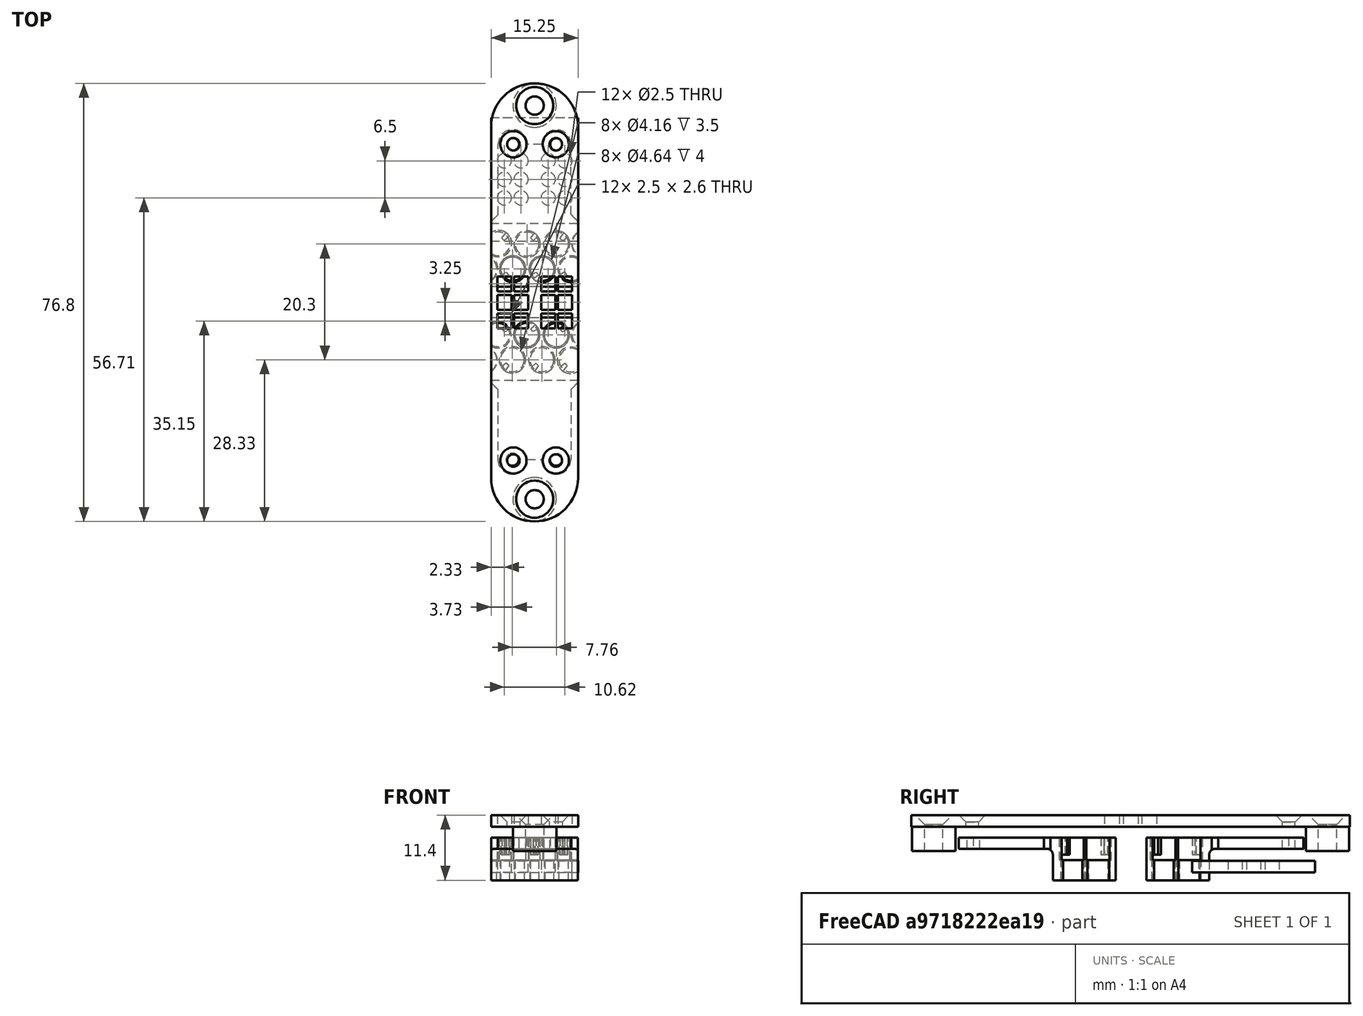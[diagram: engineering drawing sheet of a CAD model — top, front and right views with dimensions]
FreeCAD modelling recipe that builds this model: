
FCSTD DOCUMENT  (FreeCAD 0.16R6706 (Git))
Label: BrailleCell
License: All rights reserved
LicenseURL: http://en.wikipedia.org/wiki/All_rights_reserved
objects: Sketcher::SketchObject×11, PartDesign::Pad×11, PartDesign::Chamfer×5, Part::MultiFuse×5, Mesh::Feature×4, Part::Box×2, Part::Cut×2, PartDesign::Fillet×2
note: 49 computed .brp shape members not serialized (recipe doc carries the construction recipe); baked Part::Feature solids carry a one-line shape summary decoded from their .brp

FEATURE [Sketcher::SketchObject] Sketch001
  sketch-geometry (12):
    g0: LineSegment StartX=0 StartY=0 StartZ=0 EndX=15.232 EndY=0 EndZ=0
    g1: LineSegment StartX=15.232 StartY=0 StartZ=0 EndX=15.232 EndY=-20 EndZ=0
    g2: LineSegment StartX=15.232 StartY=-20 StartZ=0 EndX=0 EndY=-20 EndZ=0
    g3: LineSegment StartX=0 StartY=-20 StartZ=0 EndX=0 EndY=0 EndZ=0
    g4: Circle CenterX=3.8995 CenterY=-16.9419 CenterZ=0 NormalX=0 NormalY=0 NormalZ=1 Radius=1.1
    g5: Circle CenterX=11.3325 CenterY=-16.9419 CenterZ=0 NormalX=0 NormalY=0 NormalZ=1 Radius=1.1
    g6: LineSegment StartX=0 StartY=21.56 StartZ=0 EndX=15.232 EndY=21.56 EndZ=0
    g7: LineSegment StartX=15.232 StartY=21.56 StartZ=0 EndX=15.232 EndY=41.56 EndZ=0
    g8: LineSegment StartX=15.232 StartY=41.56 StartZ=0 EndX=0 EndY=41.56 EndZ=0
    g9: LineSegment StartX=0 StartY=41.56 StartZ=0 EndX=0 EndY=21.56 EndZ=0
    g10: Circle CenterX=3.8995 CenterY=38.5019 CenterZ=0 NormalX=0 NormalY=0 NormalZ=1 Radius=1.1
    g11: Circle CenterX=11.3325 CenterY=38.5019 CenterZ=0 NormalX=0 NormalY=0 NormalZ=1 Radius=1.1
  constraints (34):
    c: Coincident(g0,g1)
    c: Coincident(g1,g2)
    c: Coincident(g2,g3)
    c: Coincident(g3,g0)
    c: Horizontal(g0)
    c: Horizontal(g2)
    c: Vertical(g1)
    c: Vertical(g3)
    c: DistanceX(g-1,g0) = 15.232
    c: DistanceY(g2,g-1) = 20
    c: DistanceY(g4,g-1) = 16.9419
    c: Radius(g4) = 1.1
    c: DistanceY(g5,g-1) = 16.9419
    c: Radius(g5) = 1.1
    c: Coincident(g6,g7)
    c: Coincident(g7,g8)
    c: Coincident(g8,g9)
    c: Coincident(g9,g6)
    c: Horizontal(g6)
    c: Horizontal(g8)
    c: Vertical(g7)
    c: Vertical(g9)
    c: PointOnObject(g6,g-2)
    c: DistanceX(g6,g6) = 15.232
    c: DistanceY(g6,g7) = 20
    c: Radius(g11) = 1.1
    c: Radius(g10) = 1.1
    c: DistanceY(g-1,g10) = 38.5019
    c: DistanceY(g-1,g11) = 38.5019
    c: DistanceX(g6,g10) = 3.8995
    c: DistanceX(g-1,g11) = 11.3325
    c: DistanceX(g-1,g4) = 3.8995
    c: DistanceX(g-1,g5) = 11.3325
    c: DistanceY(g-1,g6) = 21.56
FEATURE [Sketcher::SketchObject] Sketch002
  sketch-geometry (6):
    g0: ArcOfCircle CenterX=7.616 CenterY=41.56 CenterZ=0 NormalX=0 NormalY=0 NormalZ=1 Radius=7.616 StartAngle=0 EndAngle=3.14159
    g1: ArcOfCircle CenterX=7.616 CenterY=-20 CenterZ=0 NormalX=0 NormalY=0 NormalZ=1 Radius=7.616 StartAngle=3.14159 EndAngle=6.28319
    g2: Circle CenterX=7.616 CenterY=45.28 CenterZ=0 NormalX=0 NormalY=0 NormalZ=1 Radius=1.6
    g3: Circle CenterX=7.616 CenterY=-23.72 CenterZ=0 NormalX=0 NormalY=0 NormalZ=1 Radius=1.6
    g4: LineSegment StartX=0 StartY=-20 StartZ=0 EndX=15.232 EndY=-20 EndZ=0
    g5: LineSegment StartX=0 StartY=41.56 StartZ=0 EndX=15.232 EndY=41.56 EndZ=0
  constraints (20):
    c: DistanceY(g-1,g0) = 41.56
    c: DistanceY(g-1,g0) = 41.56
    c: DistanceY(g-1,g0) = 41.56
    c: DistanceX(g-1,g0) = 7.616
    c: DistanceY(g1,g-1) = 20
    c: DistanceX(g-1,g1) = 7.616
    c: Radius(g2) = 1.6
    c: DistanceY(g-1,g2) = 45.28
    c: DistanceX(g-1,g2) = 7.616
    c: DistanceX(g1,g3) = 7.616
    c: Radius(g3) = 1.6
    c: DistanceY(g3,g-1) = 23.72
    c: Coincident(g4,g1)
    c: Coincident(g4,g1)
    c: Horizontal(g4)
    c: Coincident(g5,g0)
    c: Coincident(g5,g0)
    c: DistanceX(g-1,g0) = 0
    c: DistanceX(g-1,g1) = 0
    c: DistanceY(g1,g1) = 0
FEATURE [PartDesign::Pad] Pad
  Length = 2
  Length2 = 100
  Sketch = -> Sketch002
  Type = 0
FEATURE [PartDesign::Pad] Pad001
  Length = 2
  Length2 = 100
  Sketch = -> Sketch001
  Type = 0
FEATURE [Sketcher::SketchObject] Sketch004
  sketch-geometry (16):
    g0: LineSegment StartX=0 StartY=0 StartZ=0 EndX=15.232 EndY=0 EndZ=0
    g1: LineSegment StartX=15.232 StartY=0 StartZ=0 EndX=15.232 EndY=21.56 EndZ=0
    g2: LineSegment StartX=15.232 StartY=21.56 StartZ=0 EndX=0 EndY=21.56 EndZ=0
    g3: LineSegment StartX=0 StartY=21.56 StartZ=0 EndX=0 EndY=0 EndZ=0
    g4: Circle CenterX=2.3099 CenterY=7.53 CenterZ=0 NormalX=0 NormalY=0 NormalZ=1 Radius=1.25
    g5: Circle CenterX=2.3099 CenterY=14.03 CenterZ=0 NormalX=0 NormalY=0 NormalZ=1 Radius=1.25
    g6: Circle CenterX=2.3099 CenterY=10.78 CenterZ=0 NormalX=0 NormalY=0 NormalZ=1 Radius=1.25
    g7: Circle CenterX=5.2399 CenterY=14.03 CenterZ=0 NormalX=0 NormalY=0 NormalZ=1 Radius=1.25
    g8: Circle CenterX=5.2399 CenterY=10.78 CenterZ=0 NormalX=0 NormalY=0 NormalZ=1 Radius=1.25
    g9: Circle CenterX=5.2399 CenterY=7.53 CenterZ=0 NormalX=0 NormalY=0 NormalZ=1 Radius=1.25
    g10: Circle CenterX=10 CenterY=14.03 CenterZ=0 NormalX=0 NormalY=0 NormalZ=1 Radius=1.25
    g11: Circle CenterX=10 CenterY=10.78 CenterZ=0 NormalX=0 NormalY=0 NormalZ=1 Radius=1.25
    g12: Circle CenterX=10 CenterY=7.53 CenterZ=0 NormalX=0 NormalY=0 NormalZ=1 Radius=1.25
    g13: Circle CenterX=12.93 CenterY=7.53 CenterZ=0 NormalX=0 NormalY=0 NormalZ=1 Radius=1.25
    g14: Circle CenterX=12.93 CenterY=10.78 CenterZ=0 NormalX=0 NormalY=0 NormalZ=1 Radius=1.25
    g15: Circle CenterX=12.93 CenterY=14.03 CenterZ=0 NormalX=0 NormalY=0 NormalZ=1 Radius=1.25
  constraints (47):
    c: Coincident(g0,g1)
    c: Coincident(g1,g2)
    c: Coincident(g2,g3)
    c: Coincident(g3,g0)
    c: Horizontal(g0)
    c: Horizontal(g2)
    c: Vertical(g1)
    c: Vertical(g3)
    c: Coincident(g0,g-1)
    c: DistanceX(g-1,g0) = 15.232
    c: DistanceY(g-1,g2) = 21.56
    c: DistanceX(g3,g4) = 2.3099
    c: Radius(g4) = 1.25
    c: DistanceY(g4,g6) = 3.25
    c: Radius(g6) = 1.25
    c: DistanceX(g4,g6) = 0
    c: DistanceX(g6,g5) = 0
    c: Radius(g5) = 1.25
    c: DistanceY(g6,g5) = 3.25
    c: DistanceY(g3,g6) = -10.78
    c: Radius(g9) = 1.25
    c: Radius(g8) = 1.25
    c: Radius(g7) = 1.25
    c: DistanceX(g8,g9) = 0
    c: DistanceX(g7,g8) = 0
    c: DistanceY(g8,g7) = 3.25
    c: DistanceY(g9,g8) = 3.25
    c: DistanceX(g4,g9) = 2.93
    c: DistanceY(g6,g8) = 0
    c: Radius(g15) = 1.25
    c: Radius(g10) = 1.25
    c: Radius(g11) = 1.25
    c: Radius(g14) = 1.25
    c: Radius(g12) = 1.25
    c: Radius(g13) = 1.25
    c: DistanceX(g13,g14) = 0
    c: DistanceX(g15,g14) = 0
    c: DistanceY(g14,g15) = 3.25
    c: DistanceY(g13,g14) = 3.25
    c: DistanceX(g12,g11) = 0
    c: DistanceX(g11,g10) = 0
    c: DistanceY(g11,g10) = 3.25
    c: DistanceY(g12,g11) = 3.25
    c: DistanceY(g13,g12) = 0
    c: DistanceY(g3,g11) = -10.78
    c: DistanceX(g3,g11) = 10
    c: DistanceX(g11,g14) = 2.93
FEATURE [PartDesign::Pad] Pad002
  Length = 2
  Length2 = 100
  Sketch = -> Sketch004
  Type = 0
FEATURE [PartDesign::Chamfer] Chamfer
  Base = -> Pad [Edge8]
  Size = 1.65
FEATURE [PartDesign::Chamfer] Chamfer002
  Base = -> Pad001 [Edge35,Edge32,Edge17,Edge14]
  Size = 1.2
FEATURE [PartDesign::Chamfer] Chamfer003
  Base = -> Chamfer [Edge19]
  Size = 1.65
FEATURE [Sketcher::SketchObject] Sketch005
  sketch-geometry (52):
    g0: LineSegment StartX=0 StartY=0 StartZ=0 EndX=15.232 EndY=0 EndZ=0
    g1: LineSegment StartX=15.232 StartY=0 StartZ=0 EndX=15.232 EndY=21.56 EndZ=0
    g2: LineSegment StartX=15.232 StartY=21.56 StartZ=0 EndX=0 EndY=21.56 EndZ=0
    g3: LineSegment StartX=0 StartY=21.56 StartZ=0 EndX=0 EndY=0 EndZ=0
    g4: LineSegment StartX=1.0599 StartY=12.08 StartZ=0 EndX=3.5599 EndY=12.08 EndZ=0
    g5: LineSegment StartX=3.5599 StartY=12.08 StartZ=0 EndX=3.5599 EndY=9.48 EndZ=0
    g6: LineSegment StartX=3.5599 StartY=9.48 StartZ=0 EndX=1.0599 EndY=9.48 EndZ=0
    g7: LineSegment StartX=1.0599 StartY=9.48 StartZ=0 EndX=1.0599 EndY=12.08 EndZ=0
    g8: LineSegment StartX=1.0599 StartY=15.33 StartZ=0 EndX=3.5599 EndY=15.33 EndZ=0
    g9: LineSegment StartX=3.5599 StartY=15.33 StartZ=0 EndX=3.5599 EndY=12.73 EndZ=0
    g10: LineSegment StartX=3.5599 StartY=12.73 StartZ=0 EndX=1.0599 EndY=12.73 EndZ=0
    g11: LineSegment StartX=1.0599 StartY=12.73 StartZ=0 EndX=1.0599 EndY=15.33 EndZ=0
    g12: LineSegment StartX=1.0599 StartY=8.83 StartZ=0 EndX=3.5599 EndY=8.83 EndZ=0
    g13: LineSegment StartX=3.5599 StartY=8.83 StartZ=0 EndX=3.5599 EndY=6.23 EndZ=0
    g14: LineSegment StartX=3.5599 StartY=6.23 StartZ=0 EndX=1.0599 EndY=6.23 EndZ=0
    g15: LineSegment StartX=1.0599 StartY=6.23 StartZ=0 EndX=1.0599 EndY=8.83 EndZ=0
    g16: LineSegment StartX=3.9899 StartY=15.33 StartZ=0 EndX=6.4899 EndY=15.33 EndZ=0
    g17: LineSegment StartX=6.4899 StartY=15.33 StartZ=0 EndX=6.4899 EndY=12.73 EndZ=0
    g18: LineSegment StartX=6.4899 StartY=12.73 StartZ=0 EndX=3.9899 EndY=12.73 EndZ=0
    g19: LineSegment StartX=3.9899 StartY=12.73 StartZ=0 EndX=3.9899 EndY=15.33 EndZ=0
    g20: LineSegment StartX=3.9899 StartY=12.08 StartZ=0 EndX=6.4899 EndY=12.08 EndZ=0
    g21: LineSegment StartX=6.4899 StartY=12.08 StartZ=0 EndX=6.4899 EndY=9.48 EndZ=0
    g22: LineSegment StartX=6.4899 StartY=9.48 StartZ=0 EndX=3.9899 EndY=9.48 EndZ=0
    g23: LineSegment StartX=3.9899 StartY=9.48 StartZ=0 EndX=3.9899 EndY=12.08 EndZ=0
    g24: LineSegment StartX=3.9899 StartY=8.83 StartZ=0 EndX=6.4899 EndY=8.83 EndZ=0
    g25: LineSegment StartX=6.4899 StartY=8.83 StartZ=0 EndX=6.4899 EndY=6.23 EndZ=0
    g26: LineSegment StartX=6.4899 StartY=6.23 StartZ=0 EndX=3.9899 EndY=6.23 EndZ=0
    g27: LineSegment StartX=3.9899 StartY=6.23 StartZ=0 EndX=3.9899 EndY=8.83 EndZ=0
    g28: LineSegment StartX=8.75 StartY=15.33 StartZ=0 EndX=11.25 EndY=15.33 EndZ=0
    g29: LineSegment StartX=11.25 StartY=15.33 StartZ=0 EndX=11.25 EndY=12.73 EndZ=0
    g30: LineSegment StartX=11.25 StartY=12.73 StartZ=0 EndX=8.75 EndY=12.73 EndZ=0
    g31: LineSegment StartX=8.75 StartY=12.73 StartZ=0 EndX=8.75 EndY=15.33 EndZ=0
    g32: LineSegment StartX=11.68 StartY=15.33 StartZ=0 EndX=14.18 EndY=15.33 EndZ=0
    g33: LineSegment StartX=14.18 StartY=15.33 StartZ=0 EndX=14.18 EndY=12.73 EndZ=0
    g34: LineSegment StartX=14.18 StartY=12.73 StartZ=0 EndX=11.68 EndY=12.73 EndZ=0
    g35: LineSegment StartX=11.68 StartY=12.73 StartZ=0 EndX=11.68 EndY=15.33 EndZ=0
    g36: LineSegment StartX=8.75 StartY=12.08 StartZ=0 EndX=11.25 EndY=12.08 EndZ=0
    g37: LineSegment StartX=11.25 StartY=12.08 StartZ=0 EndX=11.25 EndY=9.48 EndZ=0
    g38: LineSegment StartX=11.25 StartY=9.48 StartZ=0 EndX=8.75 EndY=9.48 EndZ=0
    g39: LineSegment StartX=8.75 StartY=9.48 StartZ=0 EndX=8.75 EndY=12.08 EndZ=0
    g40: LineSegment StartX=11.68 StartY=12.08 StartZ=0 EndX=14.18 EndY=12.08 EndZ=0
    g41: LineSegment StartX=14.18 StartY=12.08 StartZ=0 EndX=14.18 EndY=9.48 EndZ=0
    g42: LineSegment StartX=14.18 StartY=9.48 StartZ=0 EndX=11.68 EndY=9.48 EndZ=0
    g43: LineSegment StartX=11.68 StartY=9.48 StartZ=0 EndX=11.68 EndY=12.08 EndZ=0
    g44: LineSegment StartX=8.75 StartY=8.83 StartZ=0 EndX=11.25 EndY=8.83 EndZ=0
    g45: LineSegment StartX=11.25 StartY=8.83 StartZ=0 EndX=11.25 EndY=6.23 EndZ=0
    g46: LineSegment StartX=11.25 StartY=6.23 StartZ=0 EndX=8.75 EndY=6.23 EndZ=0
    g47: LineSegment StartX=8.75 StartY=6.23 StartZ=0 EndX=8.75 EndY=8.83 EndZ=0
    g48: LineSegment StartX=11.68 StartY=8.83 StartZ=0 EndX=14.18 EndY=8.83 EndZ=0
    g49: LineSegment StartX=14.18 StartY=8.83 StartZ=0 EndX=14.18 EndY=6.23 EndZ=0
    g50: LineSegment StartX=14.18 StartY=6.23 StartZ=0 EndX=11.68 EndY=6.23 EndZ=0
    g51: LineSegment StartX=11.68 StartY=6.23 StartZ=0 EndX=11.68 EndY=8.83 EndZ=0
  constraints (155):
    c: Coincident(g0,g1)
    c: Coincident(g1,g2)
    c: Coincident(g2,g3)
    c: Coincident(g3,g0)
    c: Horizontal(g0)
    c: Horizontal(g2)
    c: Vertical(g1)
    c: Vertical(g3)
    c: Coincident(g0,g-1)
    c: DistanceX(g-1,g0) = 15.232
    c: DistanceY(g-1,g2) = 21.56
    c: Coincident(g4,g5)
    c: Coincident(g5,g6)
    c: Coincident(g6,g7)
    c: Coincident(g7,g4)
    c: Horizontal(g4)
    c: Horizontal(g6)
    c: Vertical(g5)
    c: Vertical(g7)
    c: Coincident(g8,g9)
    c: Coincident(g9,g10)
    c: Coincident(g10,g11)
    c: Coincident(g11,g8)
    c: Horizontal(g8)
    c: Horizontal(g10)
    c: Vertical(g9)
    c: Vertical(g11)
    c: Coincident(g12,g13)
    c: Coincident(g13,g14)
    c: Coincident(g14,g15)
    c: Coincident(g15,g12)
    c: Horizontal(g12)
    c: Horizontal(g14)
    c: Vertical(g13)
    c: Vertical(g15)
    c: Coincident(g16,g17)
    c: Coincident(g17,g18)
    c: Coincident(g18,g19)
    c: Coincident(g19,g16)
    c: Horizontal(g16)
    c: Horizontal(g18)
    c: Vertical(g17)
    c: Vertical(g19)
    c: Coincident(g20,g21)
    c: Coincident(g21,g22)
    c: Coincident(g22,g23)
    c: Coincident(g23,g20)
    c: Horizontal(g20)
    c: Horizontal(g22)
    c: Vertical(g21)
    c: Vertical(g23)
    c: Coincident(g24,g25)
    c: Coincident(g25,g26)
    c: Coincident(g26,g27)
    c: Coincident(g27,g24)
    c: Horizontal(g24)
    c: Horizontal(g26)
    c: Vertical(g25)
    c: Vertical(g27)
    c: DistanceY(g6,g4) = 2.6
    c: DistanceY(g10,g8) = 2.6
    c: DistanceY(g14,g12) = 2.6
    c: DistanceY(g-1,g6) = 9.48
    c: DistanceY(g22,g20) = 2.6
    c: DistanceY(g18,g16) = 2.6
    c: DistanceY(g26,g24) = 2.6
    c: DistanceY(g4,g10) = 0.65
    c: DistanceY(g12,g6) = 0.65
    c: DistanceY(g24,g22) = 0.65
    c: DistanceY(g20,g18) = 0.65
    c: DistanceX(g6,g5) = 2.5
    c: DistanceX(g14,g13) = 2.5
    c: DistanceX(g10,g4) = 0
    c: DistanceX(g6,g12) = 0
    c: DistanceX(g10,g9) = 2.5
    c: DistanceX(g20,g18) = 0
    c: DistanceX(g22,g24) = 0
    c: DistanceX(g22,g21) = 2.5
    c: DistanceX(g26,g25) = 2.5
    c: DistanceX(g18,g17) = 2.5
    c: DistanceX(g5,g22) = 0.43
    c: DistanceX(g-1,g6) = 1.0599
    c: Coincident(g28,g29)
    c: Coincident(g29,g30)
    c: Coincident(g30,g31)
    c: Coincident(g31,g28)
    c: Horizontal(g28)
    c: Horizontal(g30)
    c: Vertical(g29)
    c: Vertical(g31)
    c: Coincident(g32,g33)
    c: Coincident(g33,g34)
    c: Coincident(g34,g35)
    c: Coincident(g35,g32)
    c: Horizontal(g32)
    c: Horizontal(g34)
    c: Vertical(g33)
    c: Vertical(g35)
    c: Coincident(g36,g37)
    c: Coincident(g37,g38)
    c: Coincident(g38,g39)
    c: Coincident(g39,g36)
    c: Horizontal(g36)
    c: Horizontal(g38)
    c: Vertical(g37)
    c: Vertical(g39)
    c: Coincident(g40,g41)
    c: Coincident(g41,g42)
    c: Coincident(g42,g43)
    c: Coincident(g43,g40)
    c: Horizontal(g40)
    c: Horizontal(g42)
    c: Vertical(g41)
    c: Vertical(g43)
    c: Coincident(g44,g45)
    c: Coincident(g45,g46)
    c: Coincident(g46,g47)
    c: Coincident(g47,g44)
    c: Horizontal(g44)
    c: Horizontal(g46)
    c: Vertical(g45)
    c: Vertical(g47)
    c: Coincident(g48,g49)
    c: Coincident(g49,g50)
    c: Coincident(g50,g51)
    c: Coincident(g51,g48)
    c: Horizontal(g48)
    c: Horizontal(g50)
    c: Vertical(g49)
    c: Vertical(g51)
    c: DistanceX(g-1,g38) = 8.75
    c: DistanceX(g36,g36) = 2.5
    c: DistanceX(g30,g29) = 2.5
    c: DistanceX(g44,g44) = 2.5
    c: DistanceX(g40,g40) = 2.5
    c: DistanceX(g34,g33) = 2.5
    c: DistanceX(g50,g49) = 2.5
    c: DistanceY(g46,g44) = 2.6
    c: DistanceY(g50,g48) = 2.6
    c: DistanceY(g42,g40) = 2.6
    c: DistanceY(g30,g28) = 2.6
    c: DistanceY(g34,g32) = 2.6
    c: DistanceY(g38,g36) = 2.6
    c: DistanceX(g38,g44) = 0
    c: DistanceX(g30,g36) = 0
    c: DistanceX(g34,g40) = 0
    c: DistanceX(g42,g48) = 0
    c: DistanceY(g48,g42) = 0.65
    c: DistanceY(g44,g38) = 0.65
    c: DistanceY(g40,g34) = 0.65
    c: DistanceY(g36,g30) = 0.65
    c: DistanceY(g42,g37) = 0
    c: DistanceX(g37,g42) = 0.43
    c: DistanceY(g-1,g38) = 9.48
    c: DistanceY(g22,g5) = 0
FEATURE [PartDesign::Pad] Pad003
  Length = 2
  Length2 = 100
  Sketch = -> Sketch005
  Type = 0
FEATURE [Sketcher::SketchObject] Sketch
  Placement = pos=(0,0,2) rot=(0,0,1;0rad)
  sketch-geometry (4):
    g0: Circle CenterX=7.616 CenterY=45.28 CenterZ=0 NormalX=0 NormalY=0 NormalZ=1 Radius=3.8
    g1: Circle CenterX=7.616 CenterY=45.28 CenterZ=0 NormalX=0 NormalY=0 NormalZ=1 Radius=1.6
    g2: Circle CenterX=7.616 CenterY=-23.72 CenterZ=0 NormalX=0 NormalY=0 NormalZ=1 Radius=3.8
    g3: Circle CenterX=7.616 CenterY=-23.72 CenterZ=0 NormalX=0 NormalY=0 NormalZ=1 Radius=1.6
  constraints (10):
    c: Radius(g0) = 3.8
    c: Coincident(g1,g0)
    c: Radius(g1) = 1.6
    c: DistanceX(g-1,g0) = 7.616
    c: DistanceY(g-1,g0) = 45.28
    c: Coincident(g3,g2)
    c: Radius(g2) = 3.8
    c: Radius(g3) = 1.6
    c: DistanceX(g-1,g2) = 7.616
    c: DistanceY(g2,g-1) = 23.72
FEATURE [PartDesign::Pad] Pad004
  Length = 4.3
  Length2 = 100
  Placement = pos=(0,0,2) rot=(0,0,1;0rad)
  Sketch = -> Sketch
  Type = 0
FEATURE [Mesh::Feature] Pins_3  label="Pins 1"
  Placement = pos=(-0.8,-41,6.5) rot=(0,0,1;0rad)
FEATURE [Part::MultiFuse] Fusion  label="TopPlate"
  Placement = pos=(0,0,10) rot=(1,0,0;3.14159rad)
  Shapes = -> [Chamfer002,Chamfer003,Pad003,Pad004]
FEATURE [Mesh::Feature] Pins_3001  label="Pins 2"
  Placement = pos=(16,19.5,6.5) rot=(0,0,1;3.14159rad)
FEATURE [Mesh::Feature] Lever_Old_Design_1_2  label="Lever 1"
  Placement = pos=(2.2,-19.6,6.2) rot=(0,-1,0;1.5708rad)
FEATURE [Mesh::Feature] Lever_Old_Design_1_2001  label="Lever 2"
  Placement = pos=(13.05,-1.9,6.2) rot=(0.707107,0,0.707107;3.14159rad)
FEATURE [Sketcher::SketchObject] Sketch006
  sketch-geometry (24):
    g0: LineSegment StartX=1.16719 StartY=12.6074 StartZ=0 EndX=1.16719 EndY=24.9153 EndZ=0
    g1: LineSegment StartX=6.28798 StartY=24.9169 StartZ=0 EndX=8.82572 EndY=24.9169 EndZ=0
    g2: LineSegment StartX=13.9682 StartY=12.5724 StartZ=0 EndX=13.9682 EndY=24.9342 EndZ=0
    g3: ArcOfCircle CenterX=3.72758 CenterY=24.9165 CenterZ=0 NormalX=0 NormalY=0 NormalZ=1 Radius=2.56039 StartAngle=0.000160774 EndAngle=3.14208
    g4: ArcOfCircle CenterX=11.397 CenterY=24.9235 CenterZ=0 NormalX=0 NormalY=0 NormalZ=1 Radius=2.57125 StartAngle=0.00415218 EndAngle=3.14415
    g5: Circle CenterX=3.72758 CenterY=24.9165 CenterZ=0 NormalX=0 NormalY=0 NormalZ=1 Radius=1.1
    g6: Circle CenterX=11.392 CenterY=24.9235 CenterZ=0 NormalX=0 NormalY=0 NormalZ=1 Radius=1.1
    g7: LineSegment StartX=0 StartY=0 StartZ=0 EndX=15.2 EndY=0 EndZ=0
    g8: LineSegment StartX=15.2 StartY=12.5724 StartZ=0 EndX=13.9682 EndY=12.5724 EndZ=0
    g9: LineSegment StartX=0 StartY=12.6074 StartZ=0 EndX=1.16719 EndY=12.6074 EndZ=0
    g10: Circle CenterX=3.71 CenterY=7.45 CenterZ=0 NormalX=0 NormalY=0 NormalZ=1 Radius=2.32
    g11: Circle CenterX=8.8865 CenterY=7.45 CenterZ=0 NormalX=0 NormalY=0 NormalZ=1 Radius=2.32
    g12: Circle CenterX=11.4178 CenterY=3.06406 CenterZ=0 NormalX=0 NormalY=0 NormalZ=1 Radius=2.32
    g13: Circle CenterX=6.22788 CenterY=3.05007 CenterZ=0 NormalX=0 NormalY=0 NormalZ=1 Radius=2.32
    g14: ArcOfCircle CenterX=-1.2323 CenterY=7.51766 CenterZ=0 NormalX=0 NormalY=0 NormalZ=1 Radius=2.32 StartAngle=5.27236 EndAngle=7.29401
    g15: ArcOfCircle CenterX=1.16612 CenterY=3.07188 CenterZ=0 NormalX=0 NormalY=0 NormalZ=1 Radius=2.32 StartAngle=4.18574 EndAngle=8.38063
    g16: ArcOfCircle CenterX=13.8979 CenterY=7.52681 CenterZ=0 NormalX=0 NormalY=0 NormalZ=1 Radius=2.32 StartAngle=0.974907 EndAngle=5.30828
    g17: LineSegment StartX=15.2 StartY=9.44695 StartZ=0 EndX=15.2 EndY=12.5724 EndZ=0
    g18: LineSegment StartX=15.2 StartY=5.60666 StartZ=0 EndX=15.2 EndY=5.12562 EndZ=0
    g19: LineSegment StartX=15.2 StartY=1.04863 StartZ=0 EndX=15.2 EndY=0 EndZ=0
    g20: LineSegment StartX=0 StartY=0 StartZ=0 EndX=0 EndY=1.06625 EndZ=0
    g21: LineSegment StartX=0 StartY=5.07751 StartZ=0 EndX=0 EndY=5.55199 EndZ=0
    g22: LineSegment StartX=0 StartY=9.48333 StartZ=0 EndX=0 EndY=12.6074 EndZ=0
    g23: ArcOfCircle CenterX=16.3077 CenterY=3.08713 CenterZ=0 NormalX=0 NormalY=0 NormalZ=1 Radius=2.32 StartAngle=2.06854 EndAngle=4.21464
  constraints (50):
    c: Vertical(g0)
    c: Horizontal(g1)
    c: Vertical(g2)
    c: Coincident(g3,g0)
    c: Coincident(g3,g1)
    c: Coincident(g4,g1)
    c: Coincident(g4,g2)
    c: Coincident(g5,g3)
    c: Horizontal(g7)
    c: Coincident(g7,g-1)
    c: Coincident(g8,g2)
    c: Horizontal(g8)
    c: Coincident(g9,g0)
    c: Horizontal(g9)
    c: Radius(g10) = 2.32
    c: DistanceY(g-1,g10) = 7.45
    c: DistanceX(g-1,g10) = 3.71
    c: Radius(g11) = 2.32
    c: Radius(g12) = 2.32
    c: Radius(g13) = 2.32
    c: Radius(g15) = 2.32
    c: Radius(g16) = 2.32
    c: DistanceY(g-1,g11) = 7.45
    c: Coincident(g17,g16)
    c: Coincident(g17,g8)
    c: Vertical(g17)
    c: Coincident(g18,g16)
    c: Vertical(g18)
    c: Coincident(g19,g7)
    c: Vertical(g19)
    c: Coincident(g20,g-1)
    c: Coincident(g20,g15)
    c: Vertical(g20)
    c: Coincident(g21,g15)
    c: Coincident(g21,g14)
    c: Vertical(g21)
    c: Coincident(g22,g14)
    c: Coincident(g22,g9)
    c: Vertical(g22)
    c: DistanceX(g9,g8) = 15.2
    c: DistanceX(g14,g16) = 15.2
    c: DistanceX(g-1,g7) = 15.2
    c: Coincident(g23,g18)
    c: Coincident(g23,g19)
    c: DistanceX(g-1,g14) = 0
    c: DistanceX(g-1,g15) = 0
    c: Radius(g14) = 2.32
    c: Radius(g23) = 2.32
    c: Radius(g5) = 1.1
    c: Radius(g6) = 1.1
FEATURE [PartDesign::Pad] Pad005
  Length = 4
  Length2 = 100
  Sketch = -> Sketch006
  Type = 0
FEATURE [Sketcher::SketchObject] Sketch007
  Placement = pos=(0,0,4) rot=(0,0,1;0rad)
  sketch-geometry (16):
    g0: LineSegment StartX=0 StartY=0 StartZ=0 EndX=15.2 EndY=0 EndZ=0
    g1: Circle CenterX=3.71 CenterY=7.45 CenterZ=0 NormalX=0 NormalY=0 NormalZ=1 Radius=2.08
    g2: Circle CenterX=8.8865 CenterY=7.45 CenterZ=0 NormalX=0 NormalY=0 NormalZ=1 Radius=2.08
    g3: Circle CenterX=11.4178 CenterY=3.06406 CenterZ=0 NormalX=0 NormalY=0 NormalZ=1 Radius=2.08
    g4: Circle CenterX=6.22788 CenterY=3.05007 CenterZ=0 NormalX=0 NormalY=0 NormalZ=1 Radius=2.08
    g5: ArcOfCircle CenterX=-1.29213 CenterY=7.49891 CenterZ=0 NormalX=0 NormalY=0 NormalZ=1 Radius=2.27568 StartAngle=5.31622 EndAngle=7.25015
    g6: ArcOfCircle CenterX=1.20105 CenterY=3.06417 CenterZ=0 NormalX=0 NormalY=0 NormalZ=1 Radius=2.08 StartAngle=4.09681 EndAngle=8.46956
    g7: ArcOfCircle CenterX=13.9805 CenterY=7.48824 CenterZ=0 NormalX=0 NormalY=0 NormalZ=1 Radius=2.08 StartAngle=0.944332 EndAngle=5.33885
    g8: LineSegment StartX=15.2 StartY=5.80322 StartZ=0 EndX=15.2 EndY=4.94257 EndZ=0
    g9: LineSegment StartX=15.2 StartY=1.15374 StartZ=0 EndX=15.2 EndY=0 EndZ=0
    g10: LineSegment StartX=0 StartY=0 StartZ=0 EndX=0 EndY=1.36598 EndZ=0
    g11: LineSegment StartX=0 StartY=4.76237 StartZ=0 EndX=0 EndY=5.62564 EndZ=0
    g12: ArcOfCircle CenterX=16.4748 CenterY=3.04816 CenterZ=0 NormalX=0 NormalY=0 NormalZ=1 Radius=2.28338 StartAngle=2.1631 EndAngle=4.12008
    g13: LineSegment StartX=0 StartY=11 StartZ=0 EndX=15.2 EndY=11 EndZ=0
    g14: LineSegment StartX=15.2 StartY=9.17326 StartZ=0 EndX=15.2 EndY=11 EndZ=0
    g15: LineSegment StartX=0 StartY=9.37218 StartZ=0 EndX=0 EndY=11 EndZ=0
  constraints (36):
    c: Horizontal(g0)
    c: Coincident(g0,g-1)
    c: Radius(g1) = 2.08
    c: DistanceY(g-1,g1) = 7.45
    c: DistanceX(g-1,g1) = 3.71
    c: Radius(g2) = 2.08
    c: Radius(g3) = 2.08
    c: Radius(g4) = 2.08
    c: Radius(g6) = 2.08
    c: Radius(g7) = 2.08
    c: DistanceY(g-1,g2) = 7.45
    c: Coincident(g8,g7)
    c: Vertical(g8)
    c: Coincident(g9,g0)
    c: Vertical(g9)
    c: Coincident(g10,g-1)
    c: Coincident(g10,g6)
    c: Vertical(g10)
    c: Coincident(g11,g6)
    c: Coincident(g11,g5)
    c: Vertical(g11)
    c: DistanceX(g5,g7) = 15.2
    c: DistanceX(g-1,g0) = 15.2
    c: Coincident(g12,g8)
    c: Coincident(g12,g9)
    c: DistanceX(g-1,g5) = 0
    c: DistanceX(g-1,g6) = 0
    c: Horizontal(g13)
    c: Coincident(g14,g7)
    c: Coincident(g14,g13)
    c: Vertical(g14)
    c: DistanceY(g-1,g13) = 11
    c: DistanceX(g13,g-1) = 0
    c: Coincident(g15,g5)
    c: Coincident(g15,g13)
    c: DistanceX(g13,g13) = 15.2
FEATURE [PartDesign::Pad] Pad006
  Length = 3.5
  Length2 = 100
  Placement = pos=(0,0,4) rot=(0,0,1;0rad)
  Sketch = -> Sketch007
  Type = 0
FEATURE [Sketcher::SketchObject] Sketch003
  sketch-geometry (24):
    g0: LineSegment StartX=2.37867 StartY=9.53855 StartZ=0 EndX=3.14154 EndY=8.48461 EndZ=0
    g1: LineSegment StartX=3.14154 StartY=8.48461 StartZ=0 EndX=2.60525 EndY=8.03091 EndZ=0
    g2: LineSegment StartX=2.60525 StartY=8.03091 StartZ=0 EndX=1.60386 EndY=8.87946 EndZ=0
    g3: LineSegment StartX=2.37867 StartY=9.53855 StartZ=0 EndX=1.60386 EndY=8.87946 EndZ=0
    g4: LineSegment StartX=6.78436 StartY=8.94076 StartZ=0 EndX=7.81191 EndY=8.04644 EndZ=0
    g5: LineSegment StartX=7.81191 StartY=8.04644 StartZ=0 EndX=8.27871 EndY=8.4965 EndZ=0
    g6: LineSegment StartX=8.27871 StartY=8.4965 StartZ=0 EndX=7.51318 EndY=9.56846 EndZ=0
    g7: LineSegment StartX=7.51318 StartY=9.56846 StartZ=0 EndX=6.78436 EndY=8.94076 EndZ=0
    g8: LineSegment StartX=11.6397 StartY=9.07747 StartZ=0 EndX=12.905 EndY=8.01886 EndZ=0
    g9: LineSegment StartX=12.905 StartY=8.01886 StartZ=0 EndX=13.2996 EndY=8.47427 EndZ=0
    g10: LineSegment StartX=13.2996 StartY=8.47427 StartZ=0 EndX=12.401 EndY=9.69575 EndZ=0
    g11: LineSegment StartX=12.401 StartY=9.69575 StartZ=0 EndX=11.6397 EndY=9.07747 EndZ=0
    g12: LineSegment StartX=12.1046 StartY=1.97636 StartZ=0 EndX=13.3056 EndY=0.90266 EndZ=0
    g13: LineSegment StartX=13.3056 StartY=0.90266 StartZ=0 EndX=13.8986 EndY=1.72895 EndZ=0
    g14: LineSegment StartX=13.8986 StartY=1.72895 StartZ=0 EndX=12.5452 EndY=2.53763 EndZ=0
    g15: LineSegment StartX=12.5452 StartY=2.53763 StartZ=0 EndX=12.1046 EndY=1.97636 EndZ=0
    g16: LineSegment StartX=8.70009 StartY=1.7485 StartZ=0 EndX=7.31743 EndY=2.50872 EndZ=0
    g17: LineSegment StartX=7.31743 StartY=2.50872 StartZ=0 EndX=6.93042 EndY=2.02516 EndZ=0
    g18: LineSegment StartX=6.93042 StartY=2.02516 StartZ=0 EndX=8.13703 EndY=1.0298 EndZ=0
    g19: LineSegment StartX=8.13703 StartY=1.0298 StartZ=0 EndX=8.70009 EndY=1.7485 EndZ=0
    g20: LineSegment StartX=2.27306 StartY=2.56746 StartZ=0 EndX=3.50885 EndY=1.8824 EndZ=0
    g21: LineSegment StartX=3.50885 StartY=1.8824 StartZ=0 EndX=2.89778 EndY=1.21181 EndZ=0
    g22: LineSegment StartX=2.89778 StartY=1.21181 StartZ=0 EndX=1.89388 EndY=2.05588 EndZ=0
    g23: LineSegment StartX=1.89388 StartY=2.05588 StartZ=0 EndX=2.27306 EndY=2.56746 EndZ=0
  constraints (24):
    c: Coincident(g1,g0)
    c: Coincident(g2,g1)
    c: Coincident(g3,g0)
    c: Coincident(g3,g2)
    c: Coincident(g4,g5)
    c: Coincident(g5,g6)
    c: Coincident(g6,g7)
    c: Coincident(g7,g4)
    c: Coincident(g8,g9)
    c: Coincident(g9,g10)
    c: Coincident(g10,g11)
    c: Coincident(g11,g8)
    c: Coincident(g12,g13)
    c: Coincident(g13,g14)
    c: Coincident(g14,g15)
    c: Coincident(g15,g12)
    c: Coincident(g16,g17)
    c: Coincident(g17,g18)
    c: Coincident(g18,g19)
    c: Coincident(g19,g16)
    c: Coincident(g20,g21)
    c: Coincident(g21,g22)
    c: Coincident(g22,g23)
    c: Coincident(g23,g20)
FEATURE [PartDesign::Pad] Pad007
  Length = 3
  Length2 = 100
  Sketch = -> Sketch003
  Type = 0
FEATURE [PartDesign::Chamfer] Chamfer004
  Base = -> Pad005 [Edge14,Edge35]
  Size = 1.16
FEATURE [Part::MultiFuse] Fusion001
  Shapes = -> [Chamfer004,Pad007,Pad006]
FEATURE [Part::Box] Box  label="Würfel"
  Height = 10
  Length = 15.2
  Placement = pos=(0,11,2) rot=(0,0,1;0rad)
  Width = 18
FEATURE [Part::Cut] Cut
  Base = -> Fusion001
  Tool = -> Box
FEATURE [PartDesign::Fillet] Fillet
  Base = -> Cut [Edge80]
  Radius = 1
FEATURE [Sketcher::SketchObject] Sketch008
  sketch-geometry (24):
    g0: LineSegment StartX=1.16719 StartY=12.6074 StartZ=0 EndX=1.16719 EndY=24.9153 EndZ=0
    g1: LineSegment StartX=6.28798 StartY=24.9169 StartZ=0 EndX=8.82572 EndY=24.9169 EndZ=0
    g2: LineSegment StartX=13.9682 StartY=12.5724 StartZ=0 EndX=13.9682 EndY=24.9342 EndZ=0
    g3: ArcOfCircle CenterX=3.72758 CenterY=24.9165 CenterZ=0 NormalX=0 NormalY=0 NormalZ=1 Radius=2.56039 StartAngle=0.000160774 EndAngle=3.14208
    g4: ArcOfCircle CenterX=11.397 CenterY=24.9235 CenterZ=0 NormalX=0 NormalY=0 NormalZ=1 Radius=2.57125 StartAngle=0.00415218 EndAngle=3.14415
    g5: Circle CenterX=3.72758 CenterY=24.9165 CenterZ=0 NormalX=0 NormalY=0 NormalZ=1 Radius=1.1
    g6: Circle CenterX=11.392 CenterY=24.9235 CenterZ=0 NormalX=0 NormalY=0 NormalZ=1 Radius=1.1
    g7: LineSegment StartX=0 StartY=0 StartZ=0 EndX=15.2 EndY=0 EndZ=0
    g8: LineSegment StartX=15.2 StartY=12.5724 StartZ=0 EndX=13.9682 EndY=12.5724 EndZ=0
    g9: LineSegment StartX=0 StartY=12.6074 StartZ=0 EndX=1.16719 EndY=12.6074 EndZ=0
    g10: Circle CenterX=3.71 CenterY=7.45 CenterZ=0 NormalX=0 NormalY=0 NormalZ=1 Radius=2.32
    g11: Circle CenterX=8.8865 CenterY=7.45 CenterZ=0 NormalX=0 NormalY=0 NormalZ=1 Radius=2.32
    g12: Circle CenterX=11.4178 CenterY=3.06406 CenterZ=0 NormalX=0 NormalY=0 NormalZ=1 Radius=2.32
    g13: Circle CenterX=6.22788 CenterY=3.05007 CenterZ=0 NormalX=0 NormalY=0 NormalZ=1 Radius=2.32
    g14: ArcOfCircle CenterX=-1.2323 CenterY=7.51766 CenterZ=0 NormalX=0 NormalY=0 NormalZ=1 Radius=2.32 StartAngle=5.27236 EndAngle=7.29401
    g15: ArcOfCircle CenterX=1.16612 CenterY=3.07188 CenterZ=0 NormalX=0 NormalY=0 NormalZ=1 Radius=2.32 StartAngle=4.18574 EndAngle=8.38063
    g16: ArcOfCircle CenterX=13.8979 CenterY=7.52681 CenterZ=0 NormalX=0 NormalY=0 NormalZ=1 Radius=2.32 StartAngle=0.974907 EndAngle=5.30828
    g17: LineSegment StartX=15.2 StartY=9.44695 StartZ=0 EndX=15.2 EndY=12.5724 EndZ=0
    g18: LineSegment StartX=15.2 StartY=5.60666 StartZ=0 EndX=15.2 EndY=5.12562 EndZ=0
    g19: LineSegment StartX=15.2 StartY=1.04863 StartZ=0 EndX=15.2 EndY=0 EndZ=0
    g20: LineSegment StartX=0 StartY=0 StartZ=0 EndX=0 EndY=1.06625 EndZ=0
    g21: LineSegment StartX=0 StartY=5.07751 StartZ=0 EndX=0 EndY=5.55199 EndZ=0
    g22: LineSegment StartX=0 StartY=9.48333 StartZ=0 EndX=0 EndY=12.6074 EndZ=0
    g23: ArcOfCircle CenterX=16.3077 CenterY=3.08713 CenterZ=0 NormalX=0 NormalY=0 NormalZ=1 Radius=2.32 StartAngle=2.06854 EndAngle=4.21464
  constraints (50):
    c: Vertical(g0)
    c: Horizontal(g1)
    c: Vertical(g2)
    c: Coincident(g3,g0)
    c: Coincident(g3,g1)
    c: Coincident(g4,g1)
    c: Coincident(g4,g2)
    c: Coincident(g5,g3)
    c: Horizontal(g7)
    c: Coincident(g7,g-1)
    c: Coincident(g8,g2)
    c: Horizontal(g8)
    c: Coincident(g9,g0)
    c: Horizontal(g9)
    c: Radius(g10) = 2.32
    c: DistanceY(g-1,g10) = 7.45
    c: DistanceX(g-1,g10) = 3.71
    c: Radius(g11) = 2.32
    c: Radius(g12) = 2.32
    c: Radius(g13) = 2.32
    c: Radius(g15) = 2.32
    c: Radius(g16) = 2.32
    c: DistanceY(g-1,g11) = 7.45
    c: Coincident(g17,g16)
    c: Coincident(g17,g8)
    c: Vertical(g17)
    c: Coincident(g18,g16)
    c: Vertical(g18)
    c: Coincident(g19,g7)
    c: Vertical(g19)
    c: Coincident(g20,g-1)
    c: Coincident(g20,g15)
    c: Vertical(g20)
    c: Coincident(g21,g15)
    c: Coincident(g21,g14)
    c: Vertical(g21)
    c: Coincident(g22,g14)
    c: Coincident(g22,g9)
    c: Vertical(g22)
    c: DistanceX(g9,g8) = 15.2
    c: DistanceX(g14,g16) = 15.2
    c: DistanceX(g-1,g7) = 15.2
    c: Coincident(g23,g18)
    c: Coincident(g23,g19)
    c: DistanceX(g-1,g14) = 0
    c: DistanceX(g-1,g15) = 0
    c: Radius(g14) = 2.32
    c: Radius(g23) = 2.32
    c: Radius(g5) = 1.1
    c: Radius(g6) = 1.1
FEATURE [PartDesign::Pad] Pad008
  Length = 4
  Length2 = 100
  Sketch = -> Sketch008
  Type = 0
FEATURE [Sketcher::SketchObject] Sketch009
  Placement = pos=(0,0,4) rot=(0,0,1;0rad)
  sketch-geometry (16):
    g0: LineSegment StartX=0 StartY=0 StartZ=0 EndX=15.2 EndY=0 EndZ=0
    g1: Circle CenterX=3.71 CenterY=7.45 CenterZ=0 NormalX=0 NormalY=0 NormalZ=1 Radius=2.08
    g2: Circle CenterX=8.8865 CenterY=7.45 CenterZ=0 NormalX=0 NormalY=0 NormalZ=1 Radius=2.08
    g3: Circle CenterX=11.4178 CenterY=3.06406 CenterZ=0 NormalX=0 NormalY=0 NormalZ=1 Radius=2.08
    g4: Circle CenterX=6.22788 CenterY=3.05007 CenterZ=0 NormalX=0 NormalY=0 NormalZ=1 Radius=2.08
    g5: ArcOfCircle CenterX=-1.29213 CenterY=7.49891 CenterZ=0 NormalX=0 NormalY=0 NormalZ=1 Radius=2.27568 StartAngle=5.31622 EndAngle=7.25015
    g6: ArcOfCircle CenterX=1.20105 CenterY=3.06417 CenterZ=0 NormalX=0 NormalY=0 NormalZ=1 Radius=2.08 StartAngle=4.09681 EndAngle=8.46956
    g7: ArcOfCircle CenterX=13.9805 CenterY=7.48824 CenterZ=0 NormalX=0 NormalY=0 NormalZ=1 Radius=2.08 StartAngle=0.944332 EndAngle=5.33885
    g8: LineSegment StartX=15.2 StartY=5.80322 StartZ=0 EndX=15.2 EndY=4.94257 EndZ=0
    g9: LineSegment StartX=15.2 StartY=1.15374 StartZ=0 EndX=15.2 EndY=0 EndZ=0
    g10: LineSegment StartX=0 StartY=0 StartZ=0 EndX=0 EndY=1.36598 EndZ=0
    g11: LineSegment StartX=0 StartY=4.76237 StartZ=0 EndX=0 EndY=5.62564 EndZ=0
    g12: ArcOfCircle CenterX=16.4748 CenterY=3.04816 CenterZ=0 NormalX=0 NormalY=0 NormalZ=1 Radius=2.28338 StartAngle=2.1631 EndAngle=4.12008
    g13: LineSegment StartX=0 StartY=11 StartZ=0 EndX=15.2 EndY=11 EndZ=0
    g14: LineSegment StartX=15.2 StartY=9.17326 StartZ=0 EndX=15.2 EndY=11 EndZ=0
    g15: LineSegment StartX=0 StartY=9.37218 StartZ=0 EndX=0 EndY=11 EndZ=0
  constraints (36):
    c: Horizontal(g0)
    c: Coincident(g0,g-1)
    c: Radius(g1) = 2.08
    c: DistanceY(g-1,g1) = 7.45
    c: DistanceX(g-1,g1) = 3.71
    c: Radius(g2) = 2.08
    c: Radius(g3) = 2.08
    c: Radius(g4) = 2.08
    c: Radius(g6) = 2.08
    c: Radius(g7) = 2.08
    c: DistanceY(g-1,g2) = 7.45
    c: Coincident(g8,g7)
    c: Vertical(g8)
    c: Coincident(g9,g0)
    c: Vertical(g9)
    c: Coincident(g10,g-1)
    c: Coincident(g10,g6)
    c: Vertical(g10)
    c: Coincident(g11,g6)
    c: Coincident(g11,g5)
    c: Vertical(g11)
    c: DistanceX(g5,g7) = 15.2
    c: DistanceX(g-1,g0) = 15.2
    c: Coincident(g12,g8)
    c: Coincident(g12,g9)
    c: DistanceX(g-1,g5) = 0
    c: DistanceX(g-1,g6) = 0
    c: Horizontal(g13)
    c: Coincident(g14,g7)
    c: Coincident(g14,g13)
    c: Vertical(g14)
    c: DistanceY(g-1,g13) = 11
    c: DistanceX(g13,g-1) = 0
    c: Coincident(g15,g5)
    c: Coincident(g15,g13)
    c: DistanceX(g13,g13) = 15.2
FEATURE [PartDesign::Pad] Pad009
  Length = 3.5
  Length2 = 100
  Placement = pos=(0,0,4) rot=(0,0,1;0rad)
  Sketch = -> Sketch009
  Type = 0
FEATURE [Sketcher::SketchObject] Sketch010
  sketch-geometry (24):
    g0: LineSegment StartX=2.37867 StartY=9.53855 StartZ=0 EndX=3.14154 EndY=8.48461 EndZ=0
    g1: LineSegment StartX=3.14154 StartY=8.48461 StartZ=0 EndX=2.60525 EndY=8.03091 EndZ=0
    g2: LineSegment StartX=2.60525 StartY=8.03091 StartZ=0 EndX=1.60386 EndY=8.87946 EndZ=0
    g3: LineSegment StartX=2.37867 StartY=9.53855 StartZ=0 EndX=1.60386 EndY=8.87946 EndZ=0
    g4: LineSegment StartX=6.78436 StartY=8.94076 StartZ=0 EndX=7.81191 EndY=8.04644 EndZ=0
    g5: LineSegment StartX=7.81191 StartY=8.04644 StartZ=0 EndX=8.27871 EndY=8.4965 EndZ=0
    g6: LineSegment StartX=8.27871 StartY=8.4965 StartZ=0 EndX=7.51318 EndY=9.56846 EndZ=0
    g7: LineSegment StartX=7.51318 StartY=9.56846 StartZ=0 EndX=6.78436 EndY=8.94076 EndZ=0
    g8: LineSegment StartX=11.6397 StartY=9.07747 StartZ=0 EndX=12.905 EndY=8.01886 EndZ=0
    g9: LineSegment StartX=12.905 StartY=8.01886 StartZ=0 EndX=13.2996 EndY=8.47427 EndZ=0
    g10: LineSegment StartX=13.2996 StartY=8.47427 StartZ=0 EndX=12.401 EndY=9.69575 EndZ=0
    g11: LineSegment StartX=12.401 StartY=9.69575 StartZ=0 EndX=11.6397 EndY=9.07747 EndZ=0
    g12: LineSegment StartX=12.1046 StartY=1.97636 StartZ=0 EndX=13.3056 EndY=0.90266 EndZ=0
    g13: LineSegment StartX=13.3056 StartY=0.90266 StartZ=0 EndX=13.8986 EndY=1.72895 EndZ=0
    g14: LineSegment StartX=13.8986 StartY=1.72895 StartZ=0 EndX=12.5452 EndY=2.53763 EndZ=0
    g15: LineSegment StartX=12.5452 StartY=2.53763 StartZ=0 EndX=12.1046 EndY=1.97636 EndZ=0
    g16: LineSegment StartX=8.70009 StartY=1.7485 StartZ=0 EndX=7.31743 EndY=2.50872 EndZ=0
    g17: LineSegment StartX=7.31743 StartY=2.50872 StartZ=0 EndX=6.93042 EndY=2.02516 EndZ=0
    g18: LineSegment StartX=6.93042 StartY=2.02516 StartZ=0 EndX=8.13703 EndY=1.0298 EndZ=0
    g19: LineSegment StartX=8.13703 StartY=1.0298 StartZ=0 EndX=8.70009 EndY=1.7485 EndZ=0
    g20: LineSegment StartX=2.27306 StartY=2.56746 StartZ=0 EndX=3.50885 EndY=1.8824 EndZ=0
    g21: LineSegment StartX=3.50885 StartY=1.8824 StartZ=0 EndX=2.89778 EndY=1.21181 EndZ=0
    g22: LineSegment StartX=2.89778 StartY=1.21181 StartZ=0 EndX=1.89388 EndY=2.05588 EndZ=0
    g23: LineSegment StartX=1.89388 StartY=2.05588 StartZ=0 EndX=2.27306 EndY=2.56746 EndZ=0
  constraints (24):
    c: Coincident(g1,g0)
    c: Coincident(g2,g1)
    c: Coincident(g3,g0)
    c: Coincident(g3,g2)
    c: Coincident(g4,g5)
    c: Coincident(g5,g6)
    c: Coincident(g6,g7)
    c: Coincident(g7,g4)
    c: Coincident(g8,g9)
    c: Coincident(g9,g10)
    c: Coincident(g10,g11)
    c: Coincident(g11,g8)
    c: Coincident(g12,g13)
    c: Coincident(g13,g14)
    c: Coincident(g14,g15)
    c: Coincident(g15,g12)
    c: Coincident(g16,g17)
    c: Coincident(g17,g18)
    c: Coincident(g18,g19)
    c: Coincident(g19,g16)
    c: Coincident(g20,g21)
    c: Coincident(g21,g22)
    c: Coincident(g22,g23)
    c: Coincident(g23,g20)
FEATURE [PartDesign::Pad] Pad010
  Length = 3
  Length2 = 100
  Sketch = -> Sketch010
  Type = 0
FEATURE [PartDesign::Chamfer] Chamfer005
  Base = -> Pad008 [Edge14,Edge35]
  Size = 1.16
FEATURE [Part::MultiFuse] Fusion002
  Shapes = -> [Chamfer005,Pad010,Pad009]
FEATURE [Part::Box] Box001  label="Würfel001"
  Height = 10
  Length = 15.2
  Placement = pos=(0,11,2) rot=(0,0,1;0rad)
  Width = 18
FEATURE [Part::Cut] Cut001
  Base = -> Fusion002
  Tool = -> Box001
FEATURE [PartDesign::Fillet] Fillet001
  Base = -> Cut001 [Edge80]
  Radius = 1
FEATURE [Part::MultiFuse] Fusion003  label="MotorHolder_1"
  Placement = pos=(0,-13.4,6.1) rot=(1,0,0;3.14159rad)
  Shapes = -> [Fillet,Cut]
FEATURE [Part::MultiFuse] Fusion004  label="MotorHolder_2"
  Placement = pos=(15.18,-8,6.1) rot=(0,1,0;3.14159rad)
  Shapes = -> [Cut001,Fillet001]
